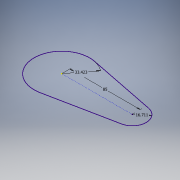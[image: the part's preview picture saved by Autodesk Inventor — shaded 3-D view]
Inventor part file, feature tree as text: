
AUTODESK INVENTOR PART (.ipt)
format: ipt  version: 2018 (Build 220112000, 112)  size: 88,064 bytes
history: native  units: mm
features: sketch x1
ambient origin geometry x8: Origin, YZ Plane, XZ Plane, XY Plane, X Axis, Y Axis, Z Axis, Center Point
feature tree (1):
  sketch  "Sketch1"  dims[d0=33.422538mm d1=85.0mm d2=16.711269mm]
